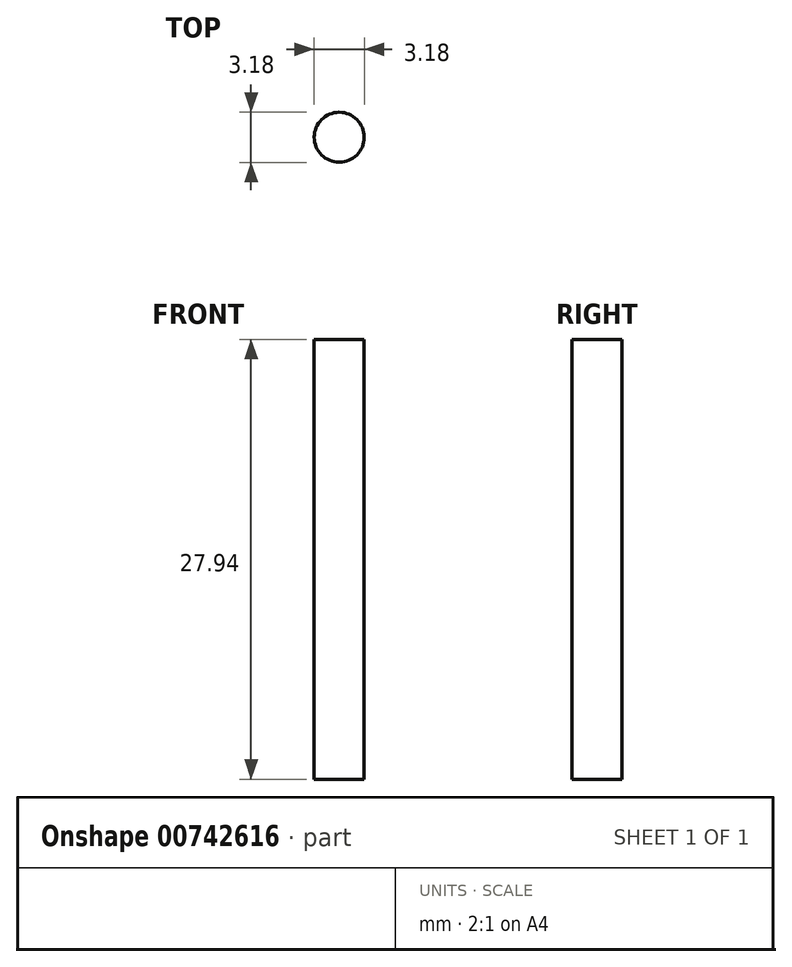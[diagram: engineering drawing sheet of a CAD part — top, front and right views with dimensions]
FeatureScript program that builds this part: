
annotation { "Feature Type Name" : "Feature", "Feature Type Description" : "" }
export const myFeature = defineFeature(function(context is Context, id is Id, definition is map)
    precondition{}
    {
        {
            var Q0;
            Q0=qCreatedBy(makeId("Top.planeOp"),FACE);
            var sketch = newSketch(context, id + "F0", { "sketchPlane" : qUnion([Q0])});
            skCircle(sketch, "E0", {"center": v(0, 0) * mm, "radius": 1.59 * mm});
            skSolve(sketch);
        }
        {
            var Q0;
            Q0=sQuery(id+"F0.wireOp",EDGE,"E0");
            extrude(context, id + "F1", {"bodyType" : ToolBodyType.SURFACE, "surfaceEntities" : qUnion([Q0]), "depth" : 25.4 * mm, "offsetDistance" : 25.4 * mm});
        }
        {
            var Q0;
            Q0 = qSketchRegion(id + "F0", true);
            extrude(context, id + "F2", {"entities" : qUnion([Q0]), "depth" : 27.94 * mm, "offsetDistance" : 25.4 * mm});
        }
    });
